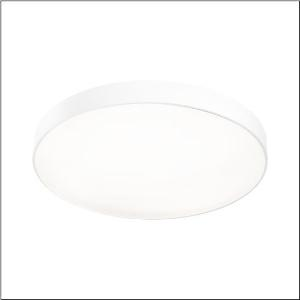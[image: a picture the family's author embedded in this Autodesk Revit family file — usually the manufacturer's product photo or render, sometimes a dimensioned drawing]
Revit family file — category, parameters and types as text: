
# Revit family: round_21_l_51mr38fd0321w
name_source: partatom
category: Lighting Fixtures
units: mm (PartAtom-declared; Revit-internal decimal feet)

## family parameters
Cut with Voids When Loaded = No
Host = Face
Light Source = No
Part Type = Normal
Room Calculation Point = No
Round Connector Dimension = Use Diameter
Shared = No

## types (1)
- Round 21 L (1 x LED, 12490 lm, 98.3 W, 3000K)
    Apparent Load = 98 VA
    CIE Flux Codes = 49 80 96 100 100
    Color Rendering = 80
    Color Temperature = 3000K
    Default Elevation = 1800 mm
    Description = Round 21 L, wall and ceiling luminaire, primary optical cover: cover, of PMMA, opal, light emission: direct distribution, primary light characteristic: symmetric, installation type: suspended mounting, surface-mounted, LED, rated luminous flux: 12.490lm, luminous efficacy: 127lm/W, light colour: 830, colour temperature: 3000K, with terminal, 5-pole, mains connection: 230V, AC, 50/60Hz, rated input power: 98W, housing, of aluminium, coated, white, diameter: 850mm, height: 62mm, protection rating (complete): IP40, insulation class (complete): insulation class I (protective earthing), certification: CE, impact resistance: IK04, permissible operating ambient temperature: -10..+35°C, packaging unit: 1 piece
    Height = 87 mm
    Lamp = 1 x LED
    Lamp Light Flux = 12490 lm
    Lamp Power = 98.3 W
    Lamp count = 1
    Length = 850 mm
    Luminous efficacy = 127 lm/W
    Manufacturer = Siteco
    ModVariant = No
    Model = 51MR38FD0321W
    Mounting Place = Ceiling
    Mounting Type = Surface mounted
    Number of Poles = 1
    OnlyDefault = Yes
    Power Factor = 1
    Product Name = Round 21 L
    Product group = wall and ceiling luminaire
    ProductGroupID = 302
    Protection Class = Protection class I
    Protection Degree = IP 40
    RLX_Detail_Level = 1
    RLX_Emergency_Light_Flux = 0 lm
    RLX_Emergency_Type = 0
    RLX_Emergency_Type_DB = No
    RlxData = <blob elided: 14993 chars, md5=e27091b1>
    Socket = socket
    Standby Power = 0 W
    System Light Flux = 12490 lm
    System Power = 98 W
    Type Comments = Product without accessories
    Type Image = l_1258320.jpg
    URL = http://relux.com
    VarID = ---
    Voltage = 0 V
    Weight = 0.00 kg
    Width = 0 mm  [stored 0 ft]

note: [stored X ft] marks values corroborated as IEEE doubles in the binary element streams (Revit-internal decimal feet)

## geometry (parser evidence)
native form markers: Sweep x12
no freeform markers — native parametric forms only
